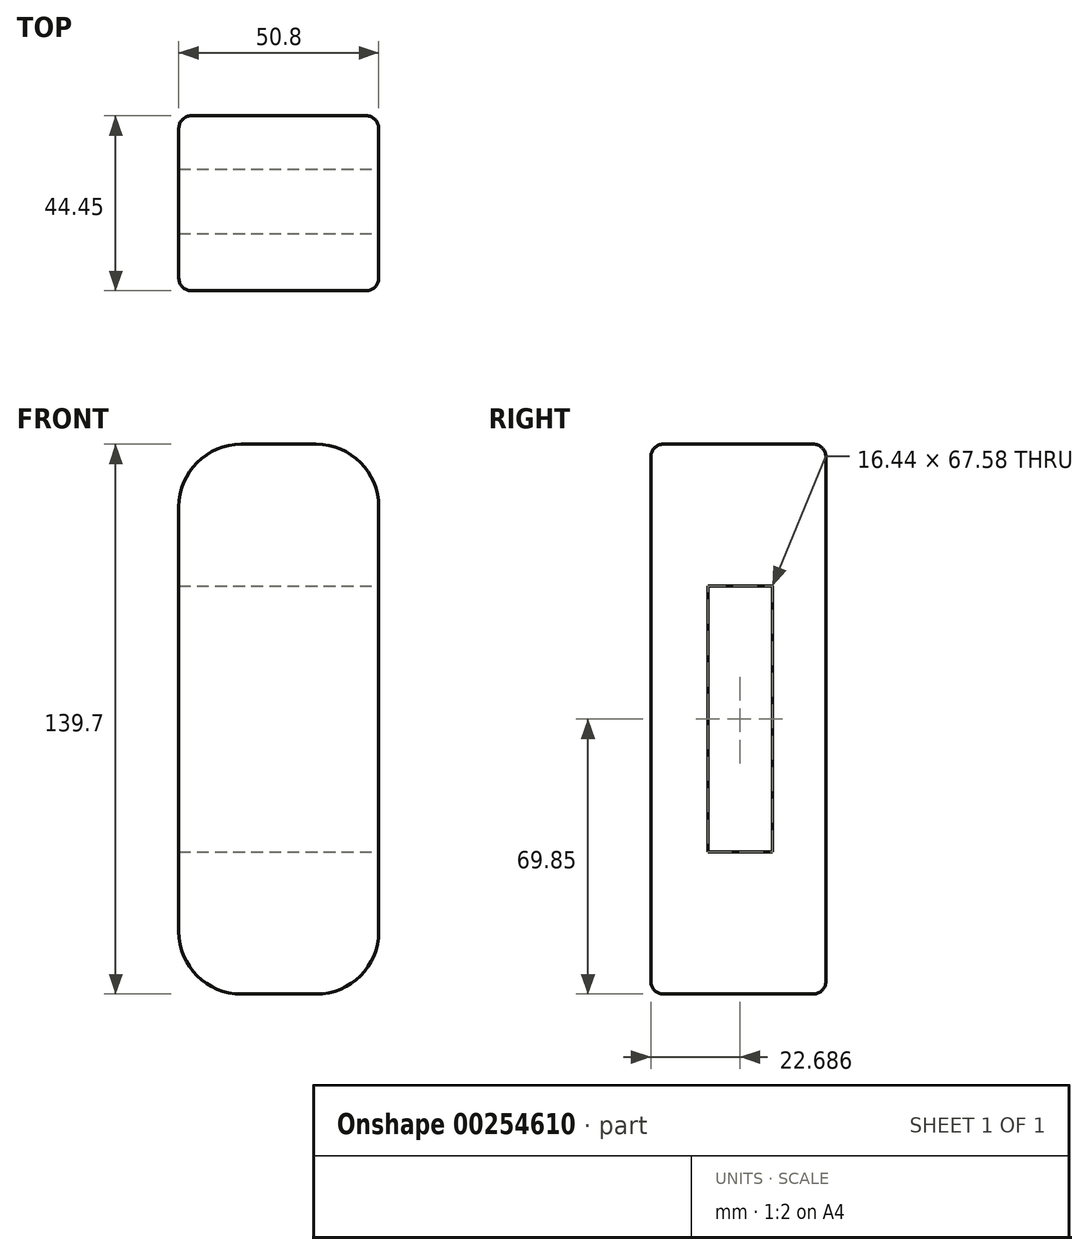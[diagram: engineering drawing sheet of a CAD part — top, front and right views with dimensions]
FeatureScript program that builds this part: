
annotation { "Feature Type Name" : "Feature", "Feature Type Description" : "" }
export const myFeature = defineFeature(function(context is Context, id is Id, definition is map)
    precondition{}
    {
        {
            var Q0;
            Q0=qCreatedBy(makeId("Front.planeOp"),FACE);
            var sketch = newSketch(context, id + "F0", { "sketchPlane" : qUnion([Q0])});
            skLineSegment(sketch, "E0.bottom", {"start": v(9.53, 69.85) * mm, "end": v(-9.52, 69.85) * mm});
            skLineSegment(sketch, "E0.top", {"start": v(9.53, -69.85) * mm, "end": v(-9.52, -69.85) * mm});
            skLineSegment(sketch, "E0.left", {"start": v(25.4, 53.98) * mm, "end": v(25.4, -53.98) * mm});
            skLineSegment(sketch, "E0.right", {"start": v(-25.4, 53.98) * mm, "end": v(-25.4, -53.98) * mm});
            skPoint(sketch, "E0.middle", {"position": v(0, 0) * mm});
            skPoint(sketch, "E1.visualSharp", {"position": v(-25.4, 69.85) * mm});
            skArc(sketch, "E1.filletArc", {"start": v(-9.52, 69.85) * mm, "mid": v(-20.75, 65.2) * mm, "end": v(-25.4, 53.98) * mm});
            skPoint(sketch, "E2.visualSharp", {"position": v(25.4, 69.85) * mm});
            skArc(sketch, "E2.filletArc", {"start": v(25.4, 53.98) * mm, "mid": v(20.75, 65.2) * mm, "end": v(9.53, 69.85) * mm});
            skPoint(sketch, "E3.visualSharp", {"position": v(25.4, -69.85) * mm});
            skArc(sketch, "E3.filletArc", {"start": v(9.53, -69.85) * mm, "mid": v(20.75, -65.2) * mm, "end": v(25.4, -53.98) * mm});
            skPoint(sketch, "E4.visualSharp", {"position": v(-25.4, -69.85) * mm});
            skArc(sketch, "E4.filletArc", {"start": v(-25.4, -53.98) * mm, "mid": v(-20.75, -65.2) * mm, "end": v(-9.52, -69.85) * mm});
            skSolve(sketch);
        }
        {
            var Q0;
            Q0 = qSketchRegion(id + "F0", true);
            extrude(context, id + "F1", {"entities" : qUnion([Q0]), "depth" : 44.45 * mm});
        }
        {
            var Q0;
            Q0=makeQuery(id+"F1.opExtrude","CAP_EDGE",EDGE,{"disambiguationData":[OSD([sQuery(id+"F0.wireOp",EDGE,"E2.filletArc")])],"isStart":false});
            var Q1;
            Q1=makeQuery(id+"F1.opExtrude","CAP_EDGE",EDGE,{"disambiguationData":[OSD([sQuery(id+"F0.wireOp",EDGE,"E2.filletArc")])],"isStart":true});
            fillet(context, id + "F2", {"entities" : qUnion([Q0, Q1]), "radius" : 3.17 * mm, "tangentPropagation" : true, "allowEdgeOverflow" : false});
        }
        {
            var Q0;
            Q0=makeQuery(id+"F1.opExtrude","SWEPT_FACE",FACE,{"disambiguationData":[OSD([sQuery(id+"F0.wireOp",EDGE,"E0.left")])]});
            var sketch = newSketch(context, id + "F3", { "sketchPlane" : qUnion([Q0])});
            skLineSegment(sketch, "E5.bottom", {"start": v(-13.54, 33.8) * mm, "end": v(-29.98, 33.8) * mm});
            skLineSegment(sketch, "E5.top", {"start": v(-13.54, -33.8) * mm, "end": v(-29.98, -33.8) * mm});
            skLineSegment(sketch, "E5.left", {"start": v(-13.54, 33.8) * mm, "end": v(-13.54, -33.8) * mm});
            skLineSegment(sketch, "E5.right", {"start": v(-29.98, 33.8) * mm, "end": v(-29.98, -33.8) * mm});
            skPoint(sketch, "E5.middle", {"position": v(-21.76, 0) * mm});
            skSolve(sketch);
        }
        {
            var Q0;
            Q0=makeQuery(id+"F3.imprint","IMPRINT",FACE,{"disambiguationData":[TD([[makeQuery(id+"F3.imprint","IMPRINT",EDGE,{"derivedFrom":sQuery(id+"F3.wireOp",EDGE,"E5.bottom")}),1.0]])]});
            extrude(context, id + "F4", {"entities" : qUnion([Q0]), "operationType" : NewBodyOperationType.REMOVE, "endBound" : BoundingType.THROUGH_ALL, "oppositeDirection" : true, "depth" : 25.4 * mm});
        }
    });
